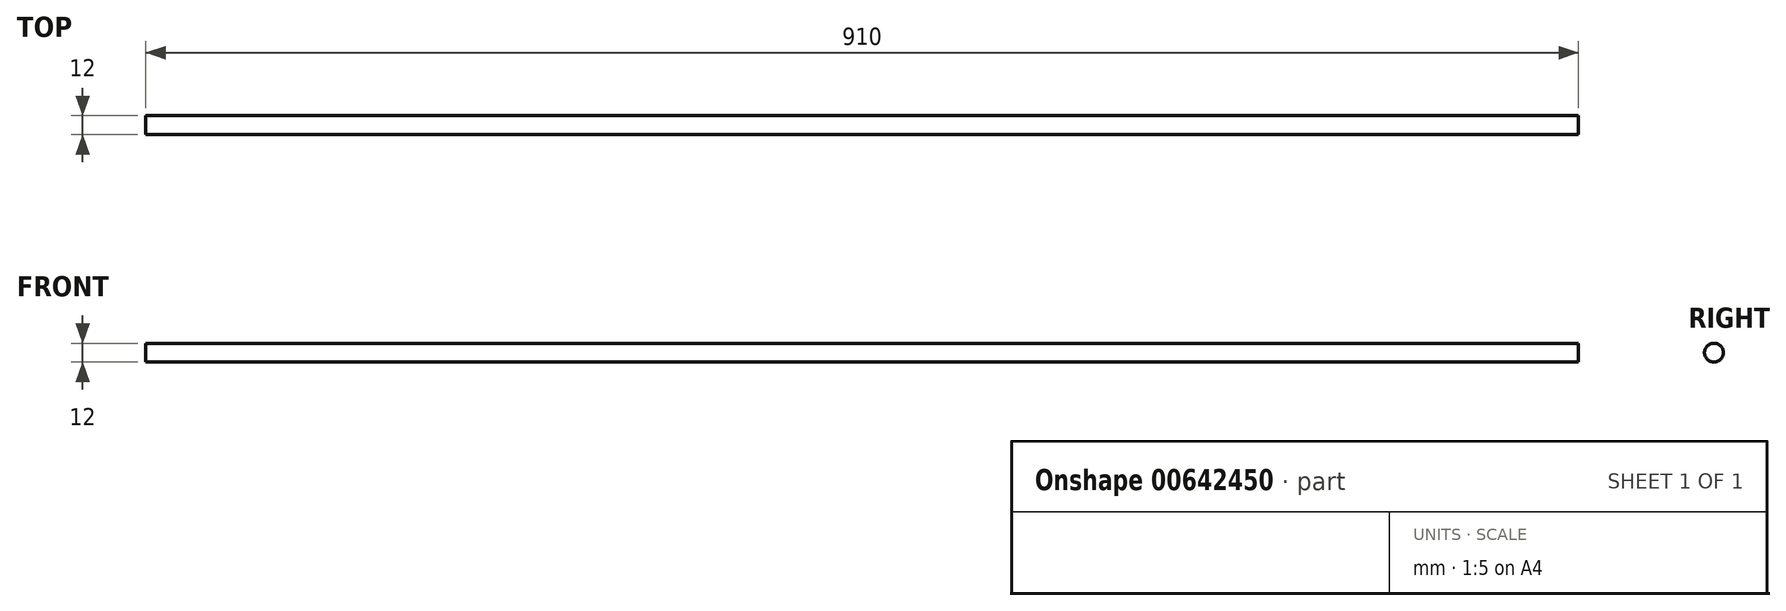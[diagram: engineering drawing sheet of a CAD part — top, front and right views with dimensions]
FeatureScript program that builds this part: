
annotation { "Feature Type Name" : "Feature", "Feature Type Description" : "" }
export const myFeature = defineFeature(function(context is Context, id is Id, definition is map)
    precondition{}
    {
        {
            var Q0;
            Q0=qCreatedBy(makeId("Right.planeOp"),FACE);
            var sketch = newSketch(context, id + "F0", { "sketchPlane" : qUnion([Q0])});
            skCircle(sketch, "E0", {"center": v(0, -0.32) * mm, "radius": 6 * mm});
            skSolve(sketch);
        }
        {
            var Q0;
            Q0=makeQuery(id+"F0.imprint","IMPRINT",FACE,{"disambiguationData":[TD([[makeQuery(id+"F0.imprint","IMPRINT",EDGE,{"derivedFrom":sQuery(id+"F0.wireOp",EDGE,"E0")}),1.0]])]});
            extrude(context, id + "F1", {"entities" : qUnion([Q0]), "depth" : 450 * mm, "offsetDistance" : 25 * mm, "hasSecondDirection" : true, "secondDirectionOppositeDirection" : true, "secondDirectionDepth" : 460 * mm});
        }
    });
